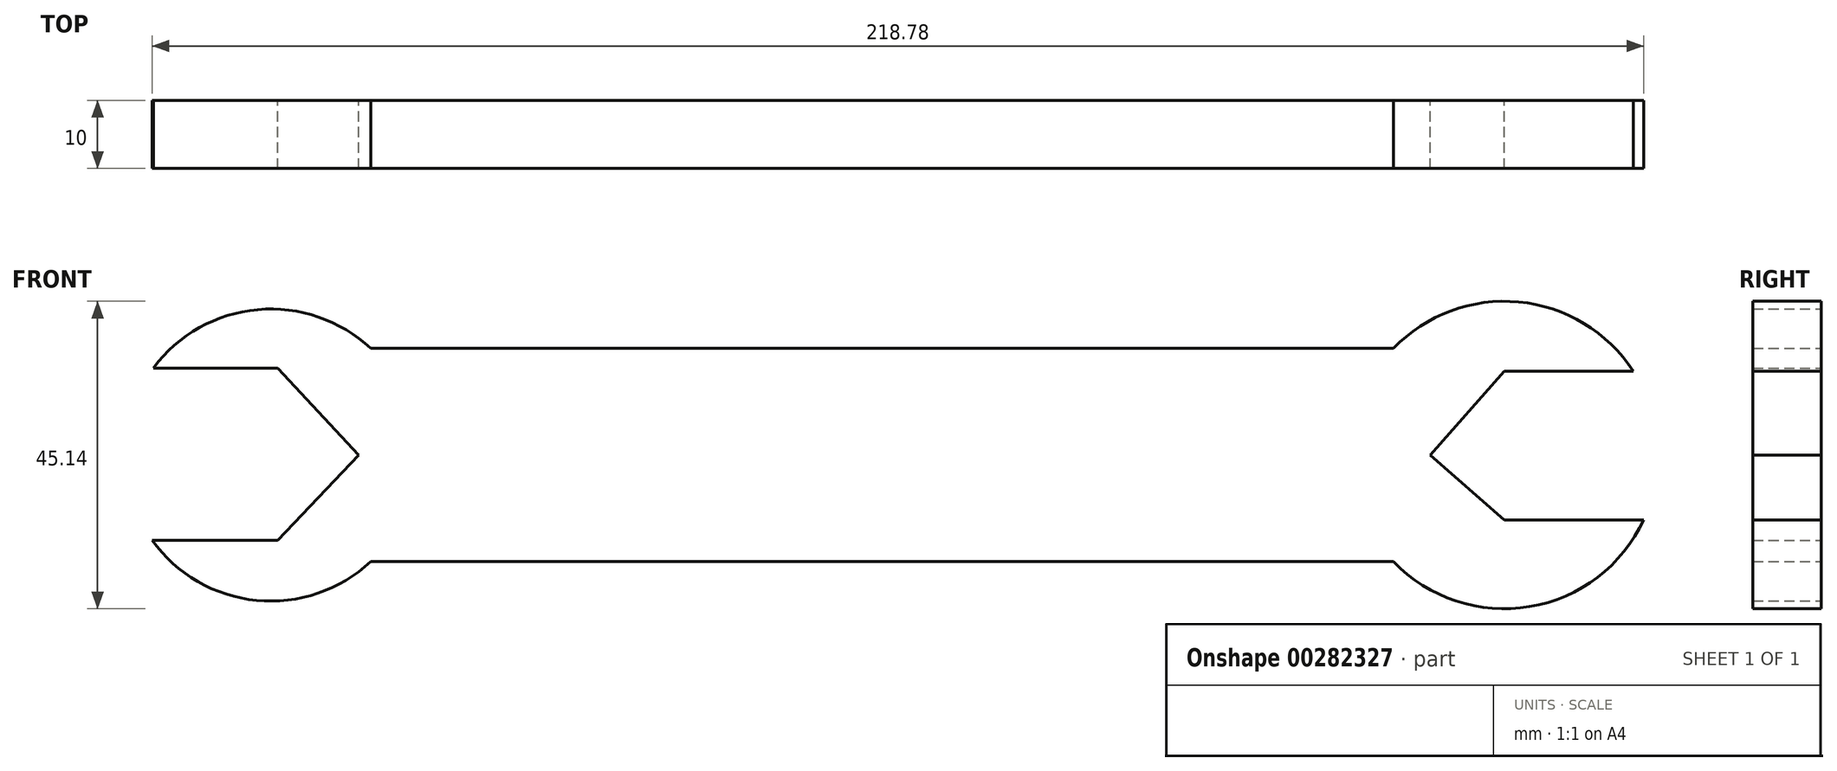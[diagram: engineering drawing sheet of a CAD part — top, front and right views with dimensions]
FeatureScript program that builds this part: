
annotation { "Feature Type Name" : "Feature", "Feature Type Description" : "" }
export const myFeature = defineFeature(function(context is Context, id is Id, definition is map)
    precondition{}
    {
        {
            var Q0;
            Q0=qCreatedBy(makeId("Front.planeOp"),FACE);
            var sketch = newSketch(context, id + "F0", { "sketchPlane" : qUnion([Q0])});
            skArc(sketch, "E0", {"start": v(18.9, 12.32) * mm, "mid": v(-22.5, -1.6) * mm, "end": v(20.46, -9.52) * mm});
            skArc(sketch, "E1", {"start": v(-198.32, -12.51) * mm, "mid": v(-159.47, -0.17) * mm, "end": v(-198.13, 12.78) * mm});
            skLineSegment(sketch, "E2", {"start": v(-180.91, 0) * mm, "end": v(0, 0) * mm, "construction": true});
            skLineSegment(sketch, "E3", {"start": v(-166.26, 15.65) * mm, "end": v(-16.26, 15.65) * mm});
            skLineSegment(sketch, "E4.MirrorCS", {"start": v(-166.26, -15.65) * mm, "end": v(-16.26, -15.65) * mm});
            skLineSegment(sketch, "E5", {"start": v(18.9, 12.32) * mm, "end": v(0, 12.32) * mm});
            skLineSegment(sketch, "E6", {"start": v(0, 12.32) * mm, "end": v(-10.83, 0) * mm});
            skLineSegment(sketch, "E7", {"start": v(-10.83, 0) * mm, "end": v(0, -9.52) * mm});
            skLineSegment(sketch, "E8", {"start": v(0, -9.52) * mm, "end": v(20.46, -9.52) * mm});
            skLineSegment(sketch, "E9", {"start": v(-198.13, 12.78) * mm, "end": v(-179.9, 12.78) * mm});
            skLineSegment(sketch, "E10", {"start": v(-179.9, 12.78) * mm, "end": v(-168.02, 0) * mm});
            skLineSegment(sketch, "E11", {"start": v(-168.02, 0) * mm, "end": v(-179.9, -12.51) * mm});
            skLineSegment(sketch, "E12", {"start": v(-179.9, -12.51) * mm, "end": v(-198.32, -12.51) * mm});
            skSolve(sketch);
        }
        {
            var Q0;
            Q0 = qSketchRegion(id + "F0", true);
            extrude(context, id + "F1", {"entities" : qUnion([Q0]), "depth" : 10 * mm});
        }
    });
